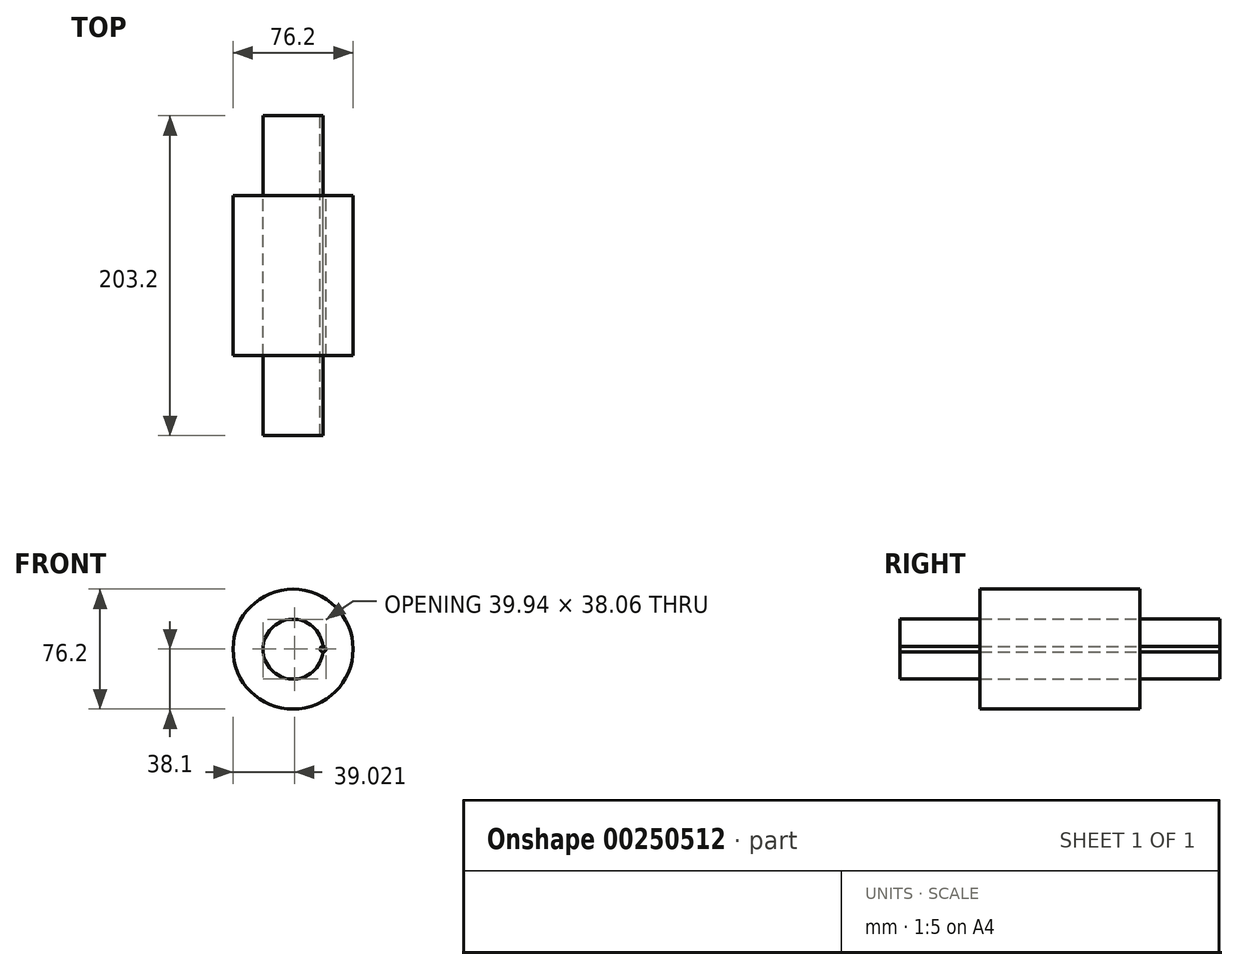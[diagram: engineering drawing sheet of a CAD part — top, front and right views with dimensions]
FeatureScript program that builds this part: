
annotation { "Feature Type Name" : "Feature", "Feature Type Description" : "" }
export const myFeature = defineFeature(function(context is Context, id is Id, definition is map)
    precondition{}
    {
        {
            var Q0;
            Q0=qCreatedBy(makeId("Front.planeOp"),FACE);
            var sketch = newSketch(context, id + "F0", { "sketchPlane" : qUnion([Q0])});
            skCircle(sketch, "E0", {"center": v(0, 0) * mm, "radius": 38.1 * mm});
            skCircle(sketch, "E1", {"center": v(0, 0) * mm, "radius": 19.05 * mm});
            skCircle(sketch, "E2", {"center": v(19.05, 0) * mm, "radius": 1.84 * mm});
            skSolve(sketch);
        }
        {
            var Q0;
            Q0=makeQuery(id+"F0.imprint","IMPRINT",FACE,{"disambiguationData":[TD([[makeQuery(id+"F0.imprint","IMPRINT",EDGE,{"derivedFrom":sQuery(id+"F0.wireOp",EDGE,"E0")}),1.0]])]});
            extrude(context, id + "F1", {"entities" : qUnion([Q0]), "endBound" : BoundingType.SYMMETRIC, "depth" : 101.6 * mm});
        }
        {
            var Q0;
            {var subQ0=sQuery(id+"F0.wireOp",EDGE,"E2");var subQ1=sQuery(id+"F0.wireOp",EDGE,"E1");var subQ2=makeQuery(id+"F0.imprint","INTERSECT",VERTEX,{"disambiguationData":[OD(0.0)],"derivedFrom":[subQ1,subQ0]});Q0=makeQuery(id+"F0.imprint","IMPRINT",FACE,{"disambiguationData":[TD([[makeQuery(id+"F0.imprint","IMPRINT",EDGE,{"disambiguationData":[TD([[subQ2,1.0]])],"derivedFrom":subQ1}),1.0]])]});}
            extrude(context, id + "F2", {"entities" : qUnion([Q0]), "endBound" : BoundingType.SYMMETRIC, "depth" : 203.2 * mm});
        }
    });
